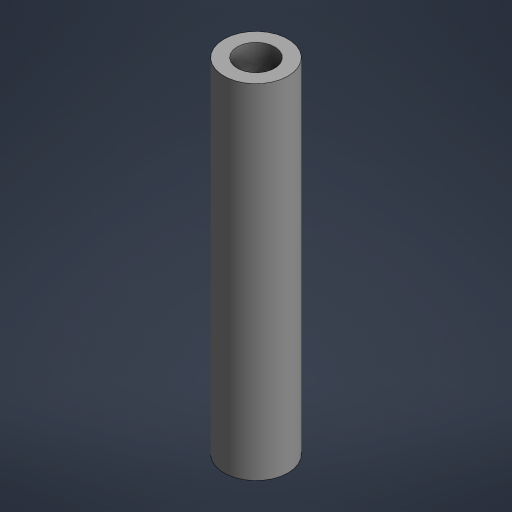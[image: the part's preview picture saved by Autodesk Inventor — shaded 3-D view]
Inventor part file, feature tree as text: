
AUTODESK INVENTOR PART (.ipt)
format: ipt  version: 2023 (Build 270158000, 158)  size: 146,432 bytes
history: native  units: mm (DEFAULTED — no unit token found)
features: extrude x1, sketch x1
ambient origin geometry x8: Origin, YZ Plane, XZ Plane, XY Plane, X Axis, Y Axis, Z Axis, Center Point
bodies: Solid1 (feature_tree)
feature tree (2):
  extrude  "Extrusion1"  Depth=47.625mm
  sketch  "Sketch1"  dims[d0=5.159375mm d1=8.89mm d2=47.625mm d3=0.0mm]
